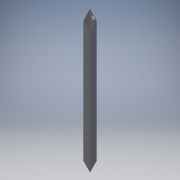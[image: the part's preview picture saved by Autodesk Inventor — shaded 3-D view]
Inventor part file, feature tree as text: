
AUTODESK INVENTOR PART (.ipt)
format: ipt  version: 2016 (Build 200138000, 138)  size: 113,152 bytes
history: native  units: in
note: dims shown in document units (in); Inventor stores cm internally (conversion verified against a paired STEP export)
features: extrude x3, sketch x3
ambient origin geometry x8: Origin, YZ Plane, XZ Plane, XY Plane, X Axis, Y Axis, Z Axis, Center Point
bodies: Solid1 (feature_tree)
feature tree (6):
  extrude  "Extrusion1"  Depth=1.0in
  extrude  "Extrusion2"  Depth=20.0in TaperAngle=0.0deg
  extrude  "Extrusion5"  Depth=1.0in
  sketch  "Sketch1"  dims[d0=1.0in d1=1.0in]
  sketch  "Sketch2"  dims[d2=0.0625in d3=20.0in d4=0.0in]
  sketch  "Sketch5"  dims[d5=0.5in d6=1.5in d7=1.0in d8=0.0in d19=0.5in d20=0.535in d21=7.385in d22=1.0in d23=0.0in]
